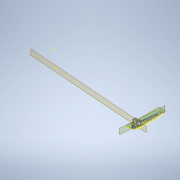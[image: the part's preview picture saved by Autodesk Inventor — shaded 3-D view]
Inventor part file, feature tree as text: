
AUTODESK INVENTOR PART (.ipt)
format: ipt  version: 2020.3 (Build 243373000, 373)  size: 381,952 bytes
history: native  units: mm
features: other x3, plane x3, sketch x2
ambient origin geometry x8: Origin, YZ Plane, XZ Plane, XY Plane, X Axis, Y Axis, Z Axis, Center Point
bodies: Solid1 (feature_tree)
feature tree (8):
  other  "LegEnd_Right_v2.ipt"
  plane  "Work Plane1"
  plane  "Work Plane2"
  plane  "Work Plane3"
  other  "Solid1::LegEnd_Right_v2.ipt"
  other  "TaggingFeature1"
  sketch  "Sketch1"  dims[d0=10.0mm]
  sketch  "Sketch3"  dims[d1=90.0deg d2=90.0deg d3=-7.5mm]
